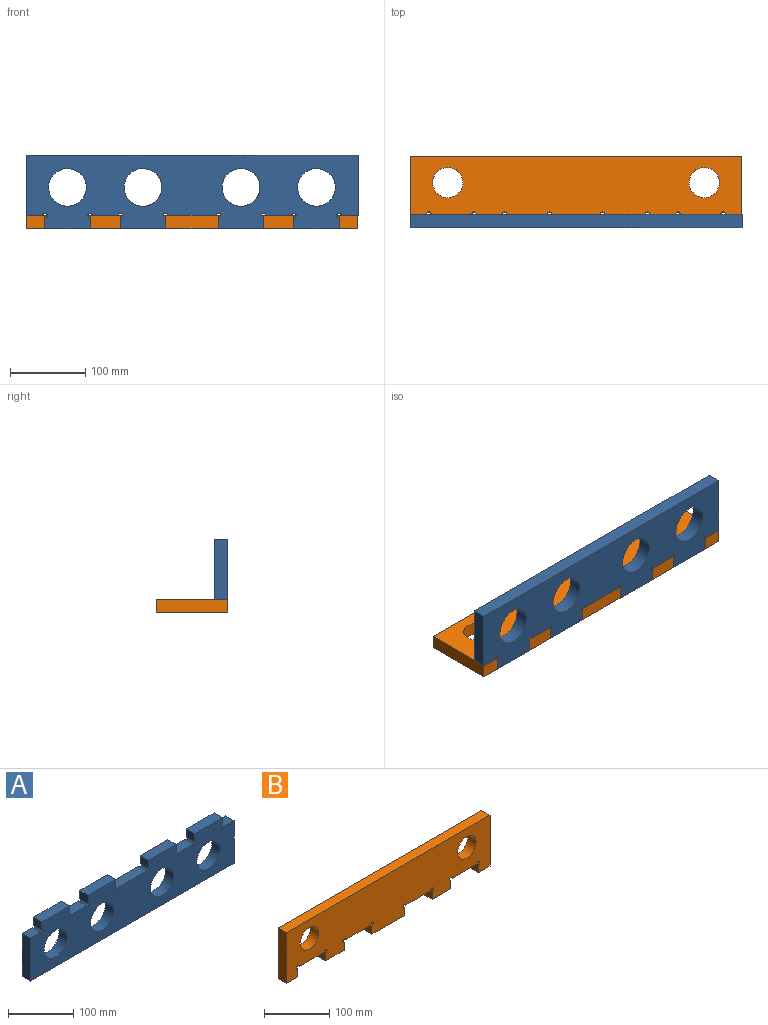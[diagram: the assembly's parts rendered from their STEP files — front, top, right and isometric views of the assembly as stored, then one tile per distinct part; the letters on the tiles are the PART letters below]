
ASSEMBLY  parts=2 mates=1
PART A: 34 faces, bbox 440x18x98 mm
  f0: plane 440x98mm, normal (0,1,0), area 31496.4mm2, adj f1,f2,f3,f4,f5,f6,f7,f8
  f1: plane 18x15mm, normal (1,0,0), area 270mm2, adj f0,f2,f26,f27
  f2: plane 60x18mm, normal (0,0,1), area 1080mm2, adj f0,f1,f3,f26
  f3: plane 18x15mm, normal (-1,0,0), area 270mm2, adj f0,f2,f4,f26
  f4: cylinder r=3mm len=18mm, axis (0,-1,0), area 254.5mm2, adj f0,f3,f5,f26
  f5: plane 34x18mm, normal (0,0,1), area 612mm2, adj f0,f4,f6,f26
  f6: cylinder r=3mm len=18mm, axis (0,-1,0), area 254.5mm2, adj f0,f5,f7,f26
  f7: plane 18x15mm, normal (1,0,0), area 270mm2, adj f0,f6,f8,f26
  f8: plane 60x18mm, normal (0,0,1), area 1080mm2, adj f0,f7,f9,f26
  f9: plane 18x15mm, normal (-1,0,0), area 270mm2, adj f0,f8,f10,f26
  f10: cylinder r=3mm len=18mm, axis (0,-1,0), area 254.5mm2, adj f0,f9,f11,f26
  f11: plane 64x18mm, normal (0,0,1), area 1152mm2, adj f0,f10,f12,f26
  f12: cylinder r=3mm len=18mm, axis (0,-1,0), area 254.5mm2, adj f0,f11,f13,f26
  f13: plane 18x15mm, normal (1,0,0), area 270mm2, adj f0,f12,f14,f26
  f14: plane 60x18mm, normal (0,0,1), area 1080mm2, adj f0,f13,f15,f26
  f15: plane 18x15mm, normal (-1,0,0), area 270mm2, adj f0,f14,f16,f26
  f16: cylinder r=3mm len=18mm, axis (0,-1,0), area 254.5mm2, adj f0,f15,f17,f26
  f17: plane 34x18mm, normal (0,0,1), area 612mm2, adj f0,f16,f18,f26
  f18: cylinder r=3mm len=18mm, axis (0,-1,0), area 254.5mm2, adj f0,f17,f19,f26
  f19: plane 18x15mm, normal (1,0,0), area 270mm2, adj f0,f18,f20,f26
  f20: plane 60x18mm, normal (0,0,1), area 1080mm2, adj f0,f19,f21,f26
  f21: plane 18x15mm, normal (-1,0,0), area 270mm2, adj f0,f20,f22,f26
  f22: cylinder r=3mm len=18mm, axis (0,-1,0), area 254.5mm2, adj f0,f21,f23,f26
  f23: plane 22x18mm, normal (0,0,1), area 396mm2, adj f0,f22,f24,f26
  f24: plane 80x18mm, normal (-1,0,0), area 1440mm2, adj f0,f23,f25,f26
  f25: plane 440x18mm, normal (0,0,-1), area 7920mm2, adj f0,f24,f26,f28
  f26: plane 440x98mm, normal (0,-1,0), area 31496.4mm2, adj f1,f2,f3,f4,f5,f6,f7,f8
  f27: cylinder r=3mm len=18mm, axis (0,-1,0), area 254.5mm2, adj f0,f1,f26,f29
  f28: plane 80x18mm, normal (1,0,0), area 1440mm2, adj f0,f25,f26,f29
  f29: plane 22x18mm, normal (0,0,1), area 396mm2, adj f0,f26,f27,f28
  f30: cylinder r=25mm len=50mm, axis (0,-1,0), area 2827.4mm2, adj f0,f26
  f31: cylinder r=25mm len=50mm, axis (0,-1,0), area 2827.4mm2, adj f0,f26
  f32: cylinder r=25mm len=50mm, axis (0,-1,0), area 2827.4mm2, adj f0,f26
  f33: cylinder r=25mm len=50mm, axis (0,-1,0), area 2827.4mm2, adj f0,f26
PART B: 32 faces, bbox 440x18x95 mm
  f0: plane 70x18mm, normal (0,0,-1), area 1260mm2, adj f1,f28,f30,f31
  f1: plane 18x15mm, normal (1,0,0), area 270mm2, adj f0,f2,f30,f31
  f2: cylinder r=3mm len=18mm, axis (0,-1,0), area 254.5mm2, adj f1,f3,f30,f31
  f3: plane 54x18mm, normal (0,0,-1), area 972mm2, adj f2,f4,f30,f31
  f4: cylinder r=3mm len=18mm, axis (0,-1,0), area 254.5mm2, adj f3,f5,f30,f31
  f5: plane 18x15mm, normal (-1,0,0), area 270mm2, adj f4,f6,f30,f31
  f6: plane 40x18mm, normal (0,0,-1), area 720mm2, adj f5,f7,f30,f31
  f7: plane 18x15mm, normal (1,0,0), area 270mm2, adj f6,f8,f30,f31
  f8: cylinder r=3mm len=18mm, axis (0,-1,0), area 254.5mm2, adj f7,f9,f30,f31
  f9: plane 54x18mm, normal (0,0,-1), area 972mm2, adj f8,f10,f30,f31
  f10: cylinder r=3mm len=18mm, axis (0,-1,0), area 254.5mm2, adj f9,f11,f30,f31
  f11: plane 18x15mm, normal (-1,0,0), area 270mm2, adj f10,f12,f30,f31
  f12: plane 25x18mm, normal (0,0,-1), area 450mm2, adj f11,f13,f30,f31
  f13: plane 95x18mm, normal (1,0,0), area 1710mm2, adj f12,f14,f30,f31
  f14: plane 440x18mm, normal (0,0,1), area 7920mm2, adj f13,f15,f30,f31
  f15: plane 95x18mm, normal (-1,0,0), area 1710mm2, adj f14,f16,f30,f31
  f16: plane 25x18mm, normal (0,0,-1), area 450mm2, adj f15,f17,f30,f31
  f17: plane 18x15mm, normal (1,0,0), area 270mm2, adj f16,f18,f30,f31
  f18: cylinder r=3mm len=18mm, axis (0,-1,0), area 254.5mm2, adj f17,f19,f30,f31
  f19: plane 54x18mm, normal (0,0,-1), area 972mm2, adj f18,f20,f30,f31
  f20: cylinder r=3mm len=18mm, axis (0,-1,0), area 254.5mm2, adj f19,f21,f30,f31
  f21: plane 18x15mm, normal (-1,0,0), area 270mm2, adj f20,f22,f30,f31
  f22: plane 40x18mm, normal (0,0,-1), area 720mm2, adj f21,f23,f30,f31
  f23: plane 18x15mm, normal (1,0,0), area 270mm2, adj f22,f24,f30,f31
  f24: cylinder r=3mm len=18mm, axis (0,-1,0), area 254.5mm2, adj f23,f25,f30,f31
  f25: plane 54x18mm, normal (0,0,-1), area 972mm2, adj f24,f26,f30,f31
  f26: cylinder r=3mm len=18mm, axis (0,-1,0), area 254.5mm2, adj f25,f28,f30,f31
  f27: cylinder r=20mm len=40mm, axis (0,-1,0), area 2261.9mm2, adj f30,f31
  f28: plane 18x15mm, normal (-1,0,0), area 270mm2, adj f0,f26,f30,f31
  f29: cylinder r=20mm len=40mm, axis (0,-1,0), area 2261.9mm2, adj f30,f31
  f30: plane 440x95mm, normal (0,1,0), area 34797.1mm2, adj f0,f1,f2,f3,f4,f5,f6,f7
  f31: plane 440x95mm, normal (0,-1,0), area 34797.1mm2, adj f0,f1,f2,f3,f4,f5,f6,f7
PLACE A rot(axis=(0,1,0),180deg) t=(567.39,-28,151.84)mm fixed
PLACE B rot(axis=(-1,0,0),90deg) t=(67.39,-88,91.82)mm
MATE slider B.f30 <-> A.f2  axis (0,0,-1) through (152.39,-10,73.82)mm
